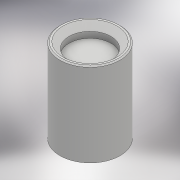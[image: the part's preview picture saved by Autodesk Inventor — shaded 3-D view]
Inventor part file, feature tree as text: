
AUTODESK INVENTOR PART (.ipt)
format: ipt  version: 2017 (Build 210142000, 142)  size: 128,000 bytes
history: native  units: mm
features: chamfer x3, extrude x2, sketch x1
ambient origin geometry x8: Origin, YZ Plane, XZ Plane, XY Plane, X Axis, Y Axis, Z Axis, Center Point
bodies: Solid1 (feature_tree)
feature tree (6):
  sketch  "Sketch1"  dims[d0=35.0mm d1=50.0mm d2=50.0mm d3=0.0mm d4=70.0mm d5=0.0mm d6=5.0mm d7=2.0mm d8=45.0deg d9=1.0mm d10=2.0mm d11=45.0deg d12=3.0mm d13=2.0mm d14=45.0deg]
  extrude  "Extrusion1"  Depth=50.0mm
  extrude  "Extrusion2"  Depth=50.0mm TaperAngle=0.0deg
  chamfer  "Chamfer1"  Distance=70.0mm
  chamfer  "Chamfer2"  Distance=5.0mm Angle=45.0deg
  chamfer  "Chamfer3"  Distance=1.0mm Angle=45.0deg
